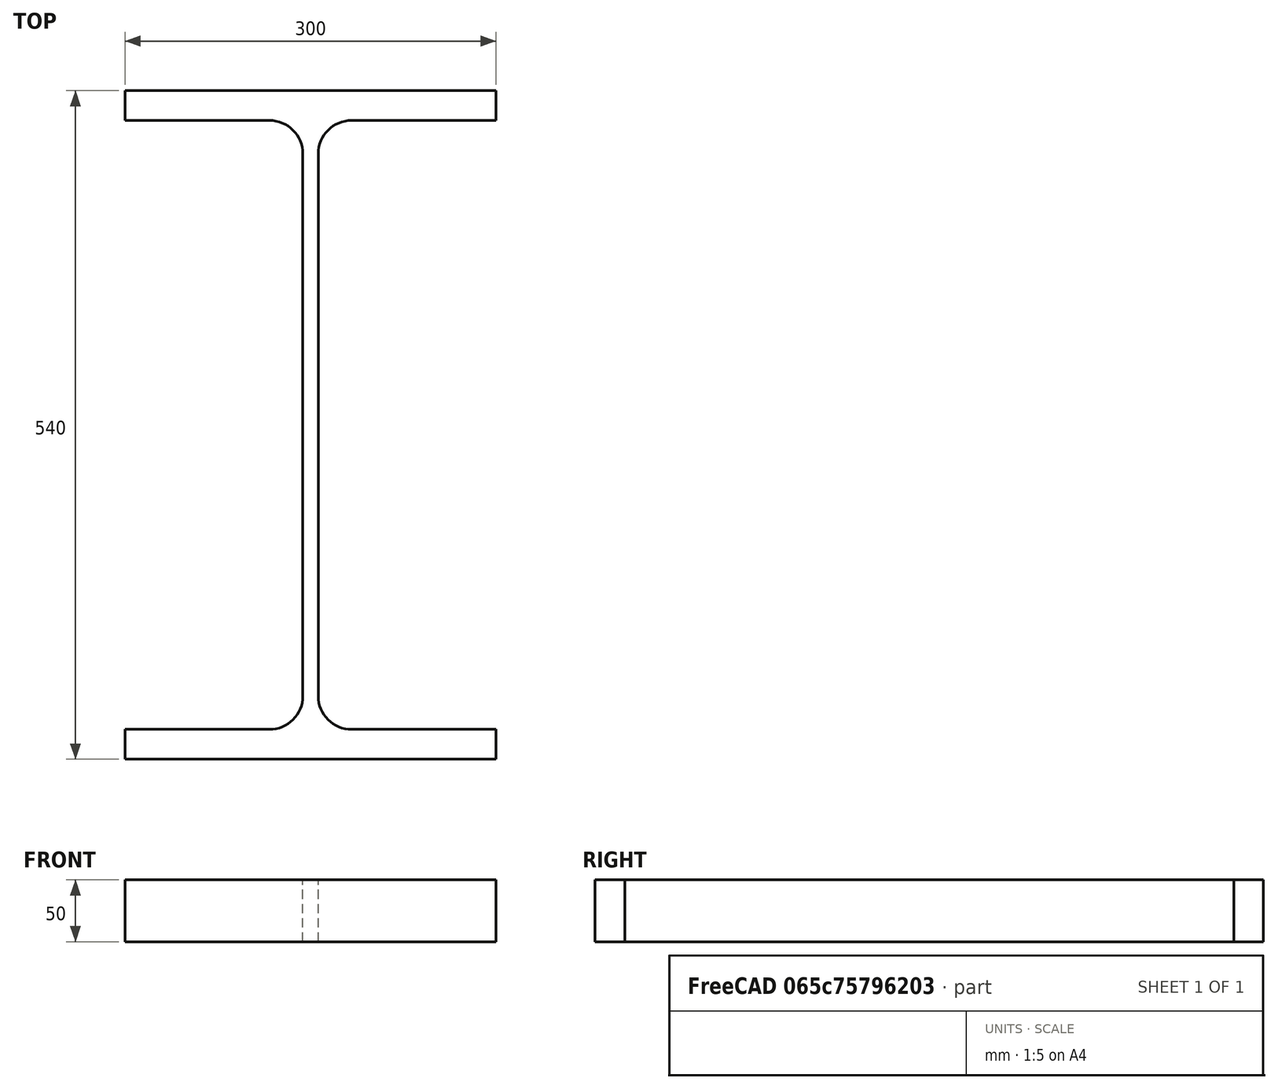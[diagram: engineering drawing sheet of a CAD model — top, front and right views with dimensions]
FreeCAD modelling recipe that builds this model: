
FCSTD DOCUMENT  (FreeCAD 0.15R4671 (Git))
Label: HE-A-Profile 550 DIN1025-3 S235JR
License: All rights reserved
LicenseURL: http://en.wikipedia.org/wiki/All_rights_reserved
objects: Sketcher::SketchObject×1, Part::Extrusion×1
note: 2 computed .brp shape members not serialized (recipe doc carries the construction recipe); baked Part::Feature solids carry a one-line shape summary decoded from their .brp

FEATURE [Sketcher::SketchObject] Sketch
  sketch-geometry (16):
    g0: LineSegment StartX=6.25 StartY=-219 StartZ=0 EndX=6.25 EndY=219 EndZ=0
    g1: LineSegment StartX=33.25 StartY=246 StartZ=0 EndX=150 EndY=246 EndZ=0
    g2: LineSegment StartX=150 StartY=246 StartZ=0 EndX=150 EndY=270 EndZ=0
    g3: LineSegment StartX=150 StartY=270 StartZ=0 EndX=-150 EndY=270 EndZ=0
    g4: LineSegment StartX=-150 StartY=270 StartZ=0 EndX=-150 EndY=246 EndZ=0
    g5: LineSegment StartX=-150 StartY=246 StartZ=0 EndX=-33.25 EndY=246 EndZ=0
    g6: LineSegment StartX=-6.25 StartY=219 StartZ=0 EndX=-6.25 EndY=-219 EndZ=0
    g7: LineSegment StartX=-33.25 StartY=-246 StartZ=0 EndX=-150 EndY=-246 EndZ=0
    g8: LineSegment StartX=-150 StartY=-246 StartZ=0 EndX=-150 EndY=-270 EndZ=0
    g9: LineSegment StartX=-150 StartY=-270 StartZ=0 EndX=150 EndY=-270 EndZ=0
    g10: LineSegment StartX=150 StartY=-270 StartZ=0 EndX=150 EndY=-246 EndZ=0
    g11: LineSegment StartX=150 StartY=-246 StartZ=0 EndX=33.25 EndY=-246 EndZ=0
    g12: ArcOfCircle CenterX=33.25 CenterY=219 CenterZ=0 NormalX=0 NormalY=0 NormalZ=1 Radius=27 StartAngle=1.5708 EndAngle=3.14159
    g13: ArcOfCircle CenterX=33.25 CenterY=-219 CenterZ=0 NormalX=0 NormalY=0 NormalZ=1 Radius=27 StartAngle=3.14159 EndAngle=4.71239
    g14: ArcOfCircle CenterX=-33.25 CenterY=219 CenterZ=0 NormalX=0 NormalY=0 NormalZ=1 Radius=27 StartAngle=0 EndAngle=1.5708
    g15: ArcOfCircle CenterX=-33.25 CenterY=-219 CenterZ=0 NormalX=0 NormalY=0 NormalZ=1 Radius=27 StartAngle=4.71239 EndAngle=6.28319
  constraints (42):
    c: Vertical(g0)
    c: Coincident(g2,g1)
    c: Vertical(g2)
    c: Coincident(g3,g2)
    c: Coincident(g4,g3)
    c: Vertical(g4)
    c: Coincident(g5,g4)
    c: Horizontal(g5)
    c: Vertical(g6)
    c: Horizontal(g7)
    c: Coincident(g8,g7)
    c: Vertical(g8)
    c: Coincident(g9,g8)
    c: Horizontal(g9)
    c: Coincident(g10,g9)
    c: Vertical(g10)
    c: Coincident(g11,g10)
    c: Horizontal(g11)
    c: Tangent(g1,g12) = 1.5708
    c: Tangent(g0,g12) = 1.5708
    c: Tangent(g0,g13) = 1.5708
    c: Tangent(g11,g13) = 1.5708
    c: Tangent(g5,g14) = 1.5708
    c: Tangent(g6,g14) = 1.5708
    c: Tangent(g6,g15) = 1.5708
    c: Tangent(g7,g15) = 1.5708
    c: Equal(g3,g9)
    c: Equal(g2,g4)
    c: Equal(g4,g8)
    c: Equal(g8,g10)
    c: Equal(g12,g14)
    c: Equal(g14,g15)
    c: Equal(g15,g13)
    c: Symmetric(g2,g3,g-2)
    c: Symmetric(g9,g8,g-2)
    c: Symmetric(g0,g6,g-2)
    c: Symmetric(g2,g9,g-1)
    c: DistanceY(g2,g9) = -540
    c: DistanceX(g3) = -300
    c: DistanceX(g0,g6) = -12.5
    c: DistanceY(g2) = 24
    c: Radius(g12) = 27
FEATURE [Part::Extrusion] Extrude  label="HE-A-Profile 550 DIN1025-3 S235JR"
  Base = -> Sketch
  Dir = (0,0,50)
  Solid = true
